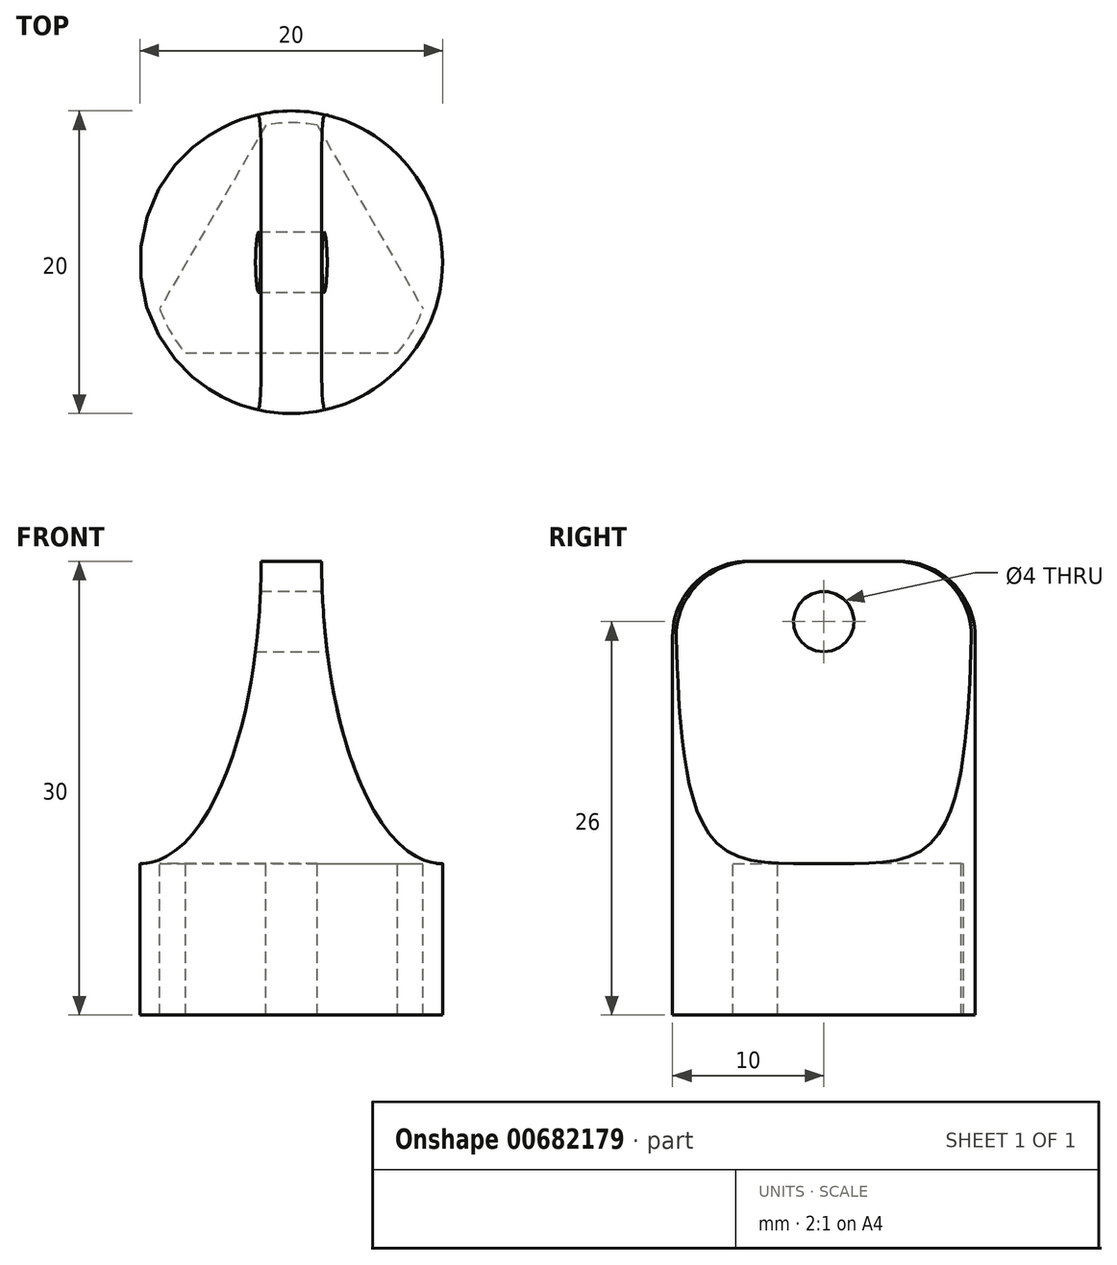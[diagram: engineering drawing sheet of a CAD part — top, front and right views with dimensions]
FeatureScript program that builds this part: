
annotation { "Feature Type Name" : "Feature", "Feature Type Description" : "" }
export const myFeature = defineFeature(function(context is Context, id is Id, definition is map)
    precondition{}
    {
        {
            assignVariable(context, id + "F0", {"name" : "ImprintDepth", "anyValue" : 10});
        }
        {
            assignVariable(context, id + "F1", {"name" : "HandleHeight", "anyValue" : 20});
        }
        {
            var Q0;
            Q0=qCreatedBy(makeId("Top.planeOp"),FACE);
            var sketch = newSketch(context, id + "F2", { "sketchPlane" : qUnion([Q0])});
            skLineSegment(sketch, "E0", {"start": v(0, 0) * mm, "end": v(0, -6) * mm});
            skLineSegment(sketch, "E1", {"start": v(0, 0) * mm, "end": v(5.2, 3) * mm});
            skLineSegment(sketch, "E2", {"start": v(0, 0) * mm, "end": v(-5.2, 3) * mm});
            skLineSegment(sketch, "E3", {"start": v(-7, -6) * mm, "end": v(7, -6) * mm});
            skLineSegment(sketch, "E4", {"start": v(1.7, 9.06) * mm, "end": v(8.7, -3.06) * mm});
            skLineSegment(sketch, "E5", {"start": v(-1.7, 9.06) * mm, "end": v(-8.7, -3.06) * mm});
            skCircle(sketch, "E6", {"center": v(0, 0) * mm, "radius": 9.22 * mm});
            skCircle(sketch, "E7", {"center": v(0, 0) * mm, "radius": 10 * mm});
            skSolve(sketch);
        }
        {
            var Q0;
            {var subQ0=sQuery(id+"F2.wireOp",EDGE,"E5");var subQ1=makeQuery(id+"F2.imprint","INTERSECT",VERTEX,{"derivedFrom":[sQuery(id+"F2.wireOp",EDGE,"E2"),subQ0]});Q0=makeQuery(id+"F2.imprint","IMPRINT",FACE,{"disambiguationData":[TD([[makeQuery(id+"F2.imprint","IMPRINT",EDGE,{"disambiguationData":[TD([[subQ1,1.0]])],"derivedFrom":subQ0}),-1.0]])]});}
            var Q1;
            {var subQ0=sQuery(id+"F2.wireOp",EDGE,"E3");var subQ1=makeQuery(id+"F2.imprint","INTERSECT",VERTEX,{"derivedFrom":[sQuery(id+"F2.wireOp",EDGE,"E0"),subQ0]});Q1=makeQuery(id+"F2.imprint","IMPRINT",FACE,{"disambiguationData":[TD([[makeQuery(id+"F2.imprint","IMPRINT",EDGE,{"disambiguationData":[TD([[subQ1,1.0]])],"derivedFrom":subQ0}),-1.0]])]});}
            var Q2;
            {var subQ0=sQuery(id+"F2.wireOp",EDGE,"E4");var subQ1=makeQuery(id+"F2.imprint","INTERSECT",VERTEX,{"derivedFrom":[sQuery(id+"F2.wireOp",EDGE,"E1"),subQ0]});Q2=makeQuery(id+"F2.imprint","IMPRINT",FACE,{"disambiguationData":[TD([[makeQuery(id+"F2.imprint","IMPRINT",EDGE,{"disambiguationData":[TD([[subQ1,1.0]])],"derivedFrom":subQ0}),1.0]])]});}
            var Q3;
            Q3=makeQuery(id+"F2.imprint","IMPRINT",FACE,{"disambiguationData":[TD([[makeQuery(id+"F2.imprint","IMPRINT",EDGE,{"derivedFrom":sQuery(id+"F2.wireOp",EDGE,"E7")}),1.0]])]});
            extrude(context, id + "F3", {"entities" : qUnion([Q0, Q1, Q2, Q3]), "depth" : -(getVariable(context, 'ImprintDepth')) * mm, "offsetDistance" : 25 * mm});
        }
        {
            var Q0;
            Q0 = qSketchRegion(id + "F2", true);
            var Q1;
            {var subQ5=sQuery(id+"F2.wireOp",EDGE,"E0");Q1=makeQuery(id+"F2.imprint","IMPRINT",FACE,{"disambiguationData":[TD([[makeQuery(id+"F2.imprint","IMPRINT",EDGE,{"derivedFrom":subQ5}),-1.0]])]});}
            var Q2;
            {var subQ0=sQuery(id+"F2.wireOp",EDGE,"E5");var subQ1=makeQuery(id+"F2.imprint","INTERSECT",VERTEX,{"derivedFrom":[sQuery(id+"F2.wireOp",EDGE,"E2"),subQ0]});Q2=makeQuery(id+"F2.imprint","IMPRINT",FACE,{"disambiguationData":[TD([[makeQuery(id+"F2.imprint","IMPRINT",EDGE,{"disambiguationData":[TD([[subQ1,1.0]])],"derivedFrom":subQ0}),-1.0]])]});}
            var Q3;
            {var subQ1=sQuery(id+"F2.wireOp",EDGE,"E1");Q3=makeQuery(id+"F2.imprint","IMPRINT",FACE,{"disambiguationData":[TD([[makeQuery(id+"F2.imprint","IMPRINT",EDGE,{"derivedFrom":subQ1}),1.0]])]});}
            var Q4;
            {var subQ1=sQuery(id+"F2.wireOp",EDGE,"E0");Q4=makeQuery(id+"F2.imprint","IMPRINT",FACE,{"disambiguationData":[TD([[makeQuery(id+"F2.imprint","IMPRINT",EDGE,{"derivedFrom":subQ1}),1.0]])]});}
            var Q5;
            {var subQ0=sQuery(id+"F2.wireOp",EDGE,"E4");var subQ1=makeQuery(id+"F2.imprint","INTERSECT",VERTEX,{"derivedFrom":[sQuery(id+"F2.wireOp",EDGE,"E1"),subQ0]});Q5=makeQuery(id+"F2.imprint","IMPRINT",FACE,{"disambiguationData":[TD([[makeQuery(id+"F2.imprint","IMPRINT",EDGE,{"disambiguationData":[TD([[subQ1,1.0]])],"derivedFrom":subQ0}),1.0]])]});}
            var Q6;
            {var subQ0=sQuery(id+"F2.wireOp",EDGE,"E3");var subQ1=makeQuery(id+"F2.imprint","INTERSECT",VERTEX,{"derivedFrom":[sQuery(id+"F2.wireOp",EDGE,"E0"),subQ0]});Q6=makeQuery(id+"F2.imprint","IMPRINT",FACE,{"disambiguationData":[TD([[makeQuery(id+"F2.imprint","IMPRINT",EDGE,{"disambiguationData":[TD([[subQ1,1.0]])],"derivedFrom":subQ0}),-1.0]])]});}
            extrude(context, id + "F4", {"entities" : qUnion([Q0, Q1, Q2, Q3, Q4, Q5, Q6]), "operationType" : NewBodyOperationType.ADD, "depth" : (getVariable(context, 'HandleHeight')) * mm, "offsetDistance" : 25 * mm});
        }
        {
            var Q0;
            Q0=qCreatedBy(makeId("Front.planeOp"),FACE);
            var sketch = newSketch(context, id + "F5", { "sketchPlane" : qUnion([Q0])});
            skLineSegment(sketch, "E8.0", {"start": v(-10, 20) * mm, "end": v(10, 20) * mm});
            skLineSegment(sketch, "E9", {"start": v(-10, -10) * mm, "end": v(-10, 20) * mm});
            skPoint(sketch, "E10", {"position": v(-10, 0) * mm});
            skLineSegment(sketch, "E11", {"start": v(0, 20) * mm, "end": v(-2, 20) * mm});
            skEllipse(sketch, "E12", {"center": v(-10, 20) * mm, "majorRadius": 8 * mm, "minorRadius": 20 * mm, "majorAxis": v(1, 0)});
            skEllipse(sketch, "E13.MirrorC", {"center": v(10, 20) * mm, "majorRadius": 8 * mm, "minorRadius": 20 * mm, "majorAxis": v(-1, 0)});
            skSolve(sketch);
        }
        {
            var Q0;
            Q0 = qSketchRegion(id + "F5", true);
            extrude(context, id + "F6", {"entities" : qUnion([Q0]), "operationType" : NewBodyOperationType.REMOVE, "endBound" : BoundingType.SYMMETRIC, "oppositeDirection" : true, "depth" : 25 * mm, "offsetDistance" : 25 * mm});
        }
        {
            var Q0;
            Q0=qCreatedBy(makeId("Right.planeOp"),FACE);
            var sketch = newSketch(context, id + "F7", { "sketchPlane" : qUnion([Q0])});
            skLineSegment(sketch, "E14.0", {"start": v(-9.8, 20) * mm, "end": v(9.8, 20) * mm});
            skCircle(sketch, "E15", {"center": v(0, 16) * mm, "radius": 2 * mm});
            skSolve(sketch);
        }
        {
            var Q0;
            Q0 = qSketchRegion(id + "F7", true);
            extrude(context, id + "F8", {"entities" : qUnion([Q0]), "operationType" : NewBodyOperationType.REMOVE, "endBound" : BoundingType.SYMMETRIC, "oppositeDirection" : true, "depth" : 25 * mm, "offsetDistance" : 25 * mm});
        }
        {
            var Q0;
            Q0=makeQuery(id+"F6.boolean.opBoolean","SPLIT",EDGE,{"disambiguationData":[OD(0.0)],"derivedFrom":makeQuery(id+"F4.opExtrude","CAP_EDGE",EDGE,{"disambiguationData":[OSD([sQuery(id+"F2.wireOp",EDGE,"E7")])],"isStart":false})});
            var Q1;
            Q1=makeQuery(id+"F6.boolean.opBoolean","SPLIT",EDGE,{"disambiguationData":[OD(1.0)],"derivedFrom":makeQuery(id+"F4.opExtrude","CAP_EDGE",EDGE,{"disambiguationData":[OSD([sQuery(id+"F2.wireOp",EDGE,"E7")])],"isStart":false})});
            fillet(context, id + "F9", {"entities" : qUnion([Q0, Q1]), "radius" : 5 * mm, "tangentPropagation" : true, "allowEdgeOverflow" : false});
        }
    });
